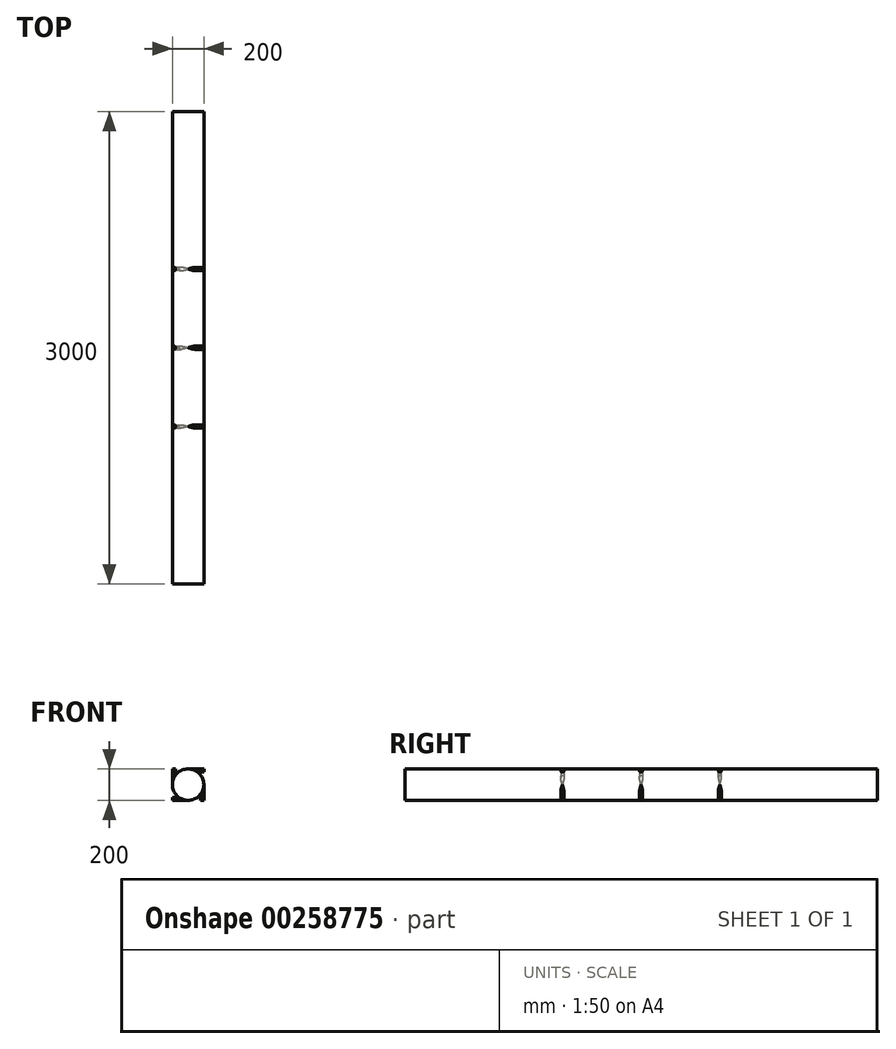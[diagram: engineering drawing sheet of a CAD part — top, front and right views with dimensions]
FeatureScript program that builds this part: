
annotation { "Feature Type Name" : "Feature", "Feature Type Description" : "" }
export const myFeature = defineFeature(function(context is Context, id is Id, definition is map)
    precondition{}
    {
        {
            var Q0;
            Q0=qCreatedBy(makeId("Front.planeOp"),FACE);
            var sketch = newSketch(context, id + "F0", { "sketchPlane" : qUnion([Q0])});
            skCircle(sketch, "E0", {"center": v(0, 0) * mm, "radius": 100 * mm});
            skSolve(sketch);
        }
        {
            var Q0;
            Q0=makeQuery(id+"F0.imprint","IMPRINT",FACE,{"disambiguationData":[TD([[makeQuery(id+"F0.imprint","IMPRINT",EDGE,{"derivedFrom":sQuery(id+"F0.wireOp",EDGE,"E0")}),1.0]])]});
            extrude(context, id + "F1", {"entities" : qUnion([Q0]), "oppositeDirection" : true, "depth" : 3000 * mm});
        }
        {
            var Q0;
            Q0=qCreatedBy(makeId("Front.planeOp"),FACE);
            cPlane(context, id + "F2", {"entities" : qUnion([Q0]), "cplaneType" : CPlaneType.OFFSET, "offset" : 1000 * mm, "oppositeDirection" : true, "width" : 150 * mm, "height" : 150 * mm});
        }
        {
            var Q0;
            Q0=qCreatedBy(makeId("Front.planeOp"),FACE);
            cPlane(context, id + "F3", {"entities" : qUnion([Q0]), "cplaneType" : CPlaneType.OFFSET, "offset" : 1500 * mm, "oppositeDirection" : true, "width" : 150 * mm, "height" : 150 * mm});
        }
        {
            var Q0;
            Q0=qCreatedBy(makeId("Front.planeOp"),FACE);
            cPlane(context, id + "F4", {"entities" : qUnion([Q0]), "cplaneType" : CPlaneType.OFFSET, "offset" : 2000 * mm, "oppositeDirection" : true, "width" : 150 * mm, "height" : 150 * mm});
        }
        {
            var Q0;
            Q0=qCreatedBy(id+"F2.planeOp",FACE);
            var sketch = newSketch(context, id + "F5", { "sketchPlane" : qUnion([Q0])});
            skLineSegment(sketch, "E1.bottom", {"start": v(0, 100) * mm, "end": v(100, 100) * mm});
            skLineSegment(sketch, "E1.top", {"start": v(0, 90) * mm, "end": v(100, 90) * mm});
            skLineSegment(sketch, "E1.left", {"start": v(0, 100) * mm, "end": v(0, 90) * mm});
            skLineSegment(sketch, "E1.right", {"start": v(100, 100) * mm, "end": v(100, 90) * mm});
            skPoint(sketch, "E2.center", {"position": v(0, 50) * mm});
            skLineSegment(sketch, "E3.1.0", {"start": v(-100, 0) * mm, "end": v(-100, 100) * mm});
            skLineSegment(sketch, "E3.1.1", {"start": v(-90, 0) * mm, "end": v(-90, 100) * mm});
            skLineSegment(sketch, "E3.1.2", {"start": v(-100, 100) * mm, "end": v(-90, 100) * mm});
            skLineSegment(sketch, "E3.1.3", {"start": v(-100, 0) * mm, "end": v(-90, 0) * mm});
            skLineSegment(sketch, "E3.2.0", {"start": v(0, -100) * mm, "end": v(-100, -100) * mm});
            skLineSegment(sketch, "E3.2.1", {"start": v(0, -90) * mm, "end": v(-100, -90) * mm});
            skLineSegment(sketch, "E3.2.2", {"start": v(-100, -100) * mm, "end": v(-100, -90) * mm});
            skLineSegment(sketch, "E3.2.3", {"start": v(0, -100) * mm, "end": v(0, -90) * mm});
            skLineSegment(sketch, "E3.3.0", {"start": v(100, 0) * mm, "end": v(100, -100) * mm});
            skLineSegment(sketch, "E3.3.1", {"start": v(90, 0) * mm, "end": v(90, -100) * mm});
            skLineSegment(sketch, "E3.3.2", {"start": v(100, -100) * mm, "end": v(90, -100) * mm});
            skLineSegment(sketch, "E3.3.3", {"start": v(100, 0) * mm, "end": v(90, 0) * mm});
            skPoint(sketch, "E3.center", {"position": v(0, 0) * mm});
            skSolve(sketch);
        }
        {
            var Q0;
            Q0=makeQuery(id+"F5.imprint","IMPRINT",FACE,{"disambiguationData":[TD([[makeQuery(id+"F5.imprint","IMPRINT",EDGE,{"derivedFrom":sQuery(id+"F5.wireOp",EDGE,"E1.bottom")}),-1.0]])]});
            var Q1;
            Q1=sQuery(id+"F5.wireOp",EDGE,"E1.top");
            revolve(context, id + "F6", {"operationType" : NewBodyOperationType.ADD, "entities" : qUnion([Q0]), "axis" : qUnion([Q1]), "revolveType" : RevolveType.FULL});
        }
        {
            var Q0;
            Q0=makeQuery(id+"F5.imprint","IMPRINT",FACE,{"disambiguationData":[TD([[makeQuery(id+"F5.imprint","IMPRINT",EDGE,{"derivedFrom":sQuery(id+"F5.wireOp",EDGE,"E3.1.0")}),-1.0]])]});
            var Q1;
            Q1=sQuery(id+"F5.wireOp",EDGE,"E3.1.1");
            revolve(context, id + "F7", {"operationType" : NewBodyOperationType.ADD, "entities" : qUnion([Q0]), "axis" : qUnion([Q1]), "revolveType" : RevolveType.FULL});
        }
        {
            var Q0;
            Q0=makeQuery(id+"F5.imprint","IMPRINT",FACE,{"disambiguationData":[TD([[makeQuery(id+"F5.imprint","IMPRINT",EDGE,{"derivedFrom":sQuery(id+"F5.wireOp",EDGE,"E3.2.0")}),-1.0]])]});
            var Q1;
            Q1=sQuery(id+"F5.wireOp",EDGE,"E3.2.1");
            revolve(context, id + "F8", {"operationType" : NewBodyOperationType.ADD, "entities" : qUnion([Q0]), "axis" : qUnion([Q1]), "revolveType" : RevolveType.FULL});
        }
        {
            var Q0;
            Q0=makeQuery(id+"F5.imprint","IMPRINT",FACE,{"disambiguationData":[TD([[makeQuery(id+"F5.imprint","IMPRINT",EDGE,{"derivedFrom":sQuery(id+"F5.wireOp",EDGE,"E3.3.0")}),-1.0]])]});
            var Q1;
            Q1=sQuery(id+"F5.wireOp",EDGE,"E3.3.1");
            revolve(context, id + "F9", {"operationType" : NewBodyOperationType.ADD, "entities" : qUnion([Q0]), "axis" : qUnion([Q1]), "revolveType" : RevolveType.FULL});
        }
        {
            var Q0;
            Q0=qCreatedBy(id+"F3.planeOp",FACE);
            var sketch = newSketch(context, id + "F10", { "sketchPlane" : qUnion([Q0])});
            skLineSegment(sketch, "E4.bottom", {"start": v(0, 100) * mm, "end": v(100, 100) * mm});
            skLineSegment(sketch, "E4.top", {"start": v(0, 90) * mm, "end": v(100, 90) * mm});
            skLineSegment(sketch, "E4.left", {"start": v(0, 100) * mm, "end": v(0, 90) * mm});
            skLineSegment(sketch, "E4.right", {"start": v(100, 100) * mm, "end": v(100, 90) * mm});
            skLineSegment(sketch, "E5.1.0", {"start": v(-100, 0) * mm, "end": v(-100, 100) * mm});
            skLineSegment(sketch, "E5.1.1", {"start": v(-90, 0) * mm, "end": v(-90, 100) * mm});
            skLineSegment(sketch, "E5.1.2", {"start": v(-100, 100) * mm, "end": v(-90, 100) * mm});
            skLineSegment(sketch, "E5.1.3", {"start": v(-100, 0) * mm, "end": v(-90, 0) * mm});
            skLineSegment(sketch, "E5.2.0", {"start": v(0, -100) * mm, "end": v(-100, -100) * mm});
            skLineSegment(sketch, "E5.2.1", {"start": v(0, -90) * mm, "end": v(-100, -90) * mm});
            skLineSegment(sketch, "E5.2.2", {"start": v(-100, -100) * mm, "end": v(-100, -90) * mm});
            skLineSegment(sketch, "E5.2.3", {"start": v(0, -100) * mm, "end": v(0, -90) * mm});
            skLineSegment(sketch, "E5.3.0", {"start": v(100, 0) * mm, "end": v(100, -100) * mm});
            skLineSegment(sketch, "E5.3.1", {"start": v(90, 0) * mm, "end": v(90, -100) * mm});
            skLineSegment(sketch, "E5.3.2", {"start": v(100, -100) * mm, "end": v(90, -100) * mm});
            skLineSegment(sketch, "E5.3.3", {"start": v(100, 0) * mm, "end": v(90, 0) * mm});
            skPoint(sketch, "E5.center", {"position": v(0, 0) * mm});
            skSolve(sketch);
        }
        {
            var Q0;
            Q0=makeQuery(id+"F10.imprint","IMPRINT",FACE,{"disambiguationData":[TD([[makeQuery(id+"F10.imprint","IMPRINT",EDGE,{"derivedFrom":sQuery(id+"F10.wireOp",EDGE,"E4.bottom")}),-1.0]])]});
            var Q1;
            Q1=sQuery(id+"F10.wireOp",EDGE,"E4.top");
            revolve(context, id + "F11", {"operationType" : NewBodyOperationType.ADD, "entities" : qUnion([Q0]), "axis" : qUnion([Q1]), "revolveType" : RevolveType.FULL});
        }
        {
            var Q0;
            Q0=makeQuery(id+"F10.imprint","IMPRINT",FACE,{"disambiguationData":[TD([[makeQuery(id+"F10.imprint","IMPRINT",EDGE,{"derivedFrom":sQuery(id+"F10.wireOp",EDGE,"E5.3.0")}),-1.0]])]});
            var Q1;
            Q1=sQuery(id+"F10.wireOp",EDGE,"E5.3.1");
            revolve(context, id + "F12", {"operationType" : NewBodyOperationType.ADD, "entities" : qUnion([Q0]), "axis" : qUnion([Q1]), "revolveType" : RevolveType.FULL});
        }
        {
            var Q0;
            Q0=makeQuery(id+"F10.imprint","IMPRINT",FACE,{"disambiguationData":[TD([[makeQuery(id+"F10.imprint","IMPRINT",EDGE,{"derivedFrom":sQuery(id+"F10.wireOp",EDGE,"E5.1.0")}),-1.0]])]});
            var Q1;
            Q1=sQuery(id+"F10.wireOp",EDGE,"E5.1.1");
            revolve(context, id + "F13", {"operationType" : NewBodyOperationType.ADD, "entities" : qUnion([Q0]), "axis" : qUnion([Q1]), "revolveType" : RevolveType.FULL});
        }
        {
            var Q0;
            Q0=makeQuery(id+"F10.imprint","IMPRINT",FACE,{"disambiguationData":[TD([[makeQuery(id+"F10.imprint","IMPRINT",EDGE,{"derivedFrom":sQuery(id+"F10.wireOp",EDGE,"E5.2.0")}),-1.0]])]});
            var Q1;
            Q1=sQuery(id+"F10.wireOp",EDGE,"E5.2.1");
            revolve(context, id + "F14", {"operationType" : NewBodyOperationType.ADD, "entities" : qUnion([Q0]), "axis" : qUnion([Q1]), "revolveType" : RevolveType.FULL});
        }
        {
            var Q0;
            Q0=qCreatedBy(id+"F4.planeOp",FACE);
            var sketch = newSketch(context, id + "F15", { "sketchPlane" : qUnion([Q0])});
            skLineSegment(sketch, "E6", {"start": v(0, 100) * mm, "end": v(100, 100) * mm});
            skLineSegment(sketch, "E7", {"start": v(100, 100) * mm, "end": v(100, 90) * mm});
            skLineSegment(sketch, "E8", {"start": v(100, 90) * mm, "end": v(0, 90) * mm});
            skLineSegment(sketch, "E9", {"start": v(0, 90) * mm, "end": v(0, 100) * mm});
            skLineSegment(sketch, "E10.1.0", {"start": v(-90, 0) * mm, "end": v(-100, 0) * mm});
            skLineSegment(sketch, "E10.1.1", {"start": v(-90, 100) * mm, "end": v(-90, 0) * mm});
            skLineSegment(sketch, "E10.1.2", {"start": v(-100, 0) * mm, "end": v(-100, 100) * mm});
            skLineSegment(sketch, "E10.1.3", {"start": v(-100, 100) * mm, "end": v(-90, 100) * mm});
            skLineSegment(sketch, "E10.2.0", {"start": v(0, -90) * mm, "end": v(0, -100) * mm});
            skLineSegment(sketch, "E10.2.1", {"start": v(-100, -90) * mm, "end": v(0, -90) * mm});
            skLineSegment(sketch, "E10.2.2", {"start": v(0, -100) * mm, "end": v(-100, -100) * mm});
            skLineSegment(sketch, "E10.2.3", {"start": v(-100, -100) * mm, "end": v(-100, -90) * mm});
            skLineSegment(sketch, "E10.3.0", {"start": v(90, 0) * mm, "end": v(100, 0) * mm});
            skLineSegment(sketch, "E10.3.1", {"start": v(90, -100) * mm, "end": v(90, 0) * mm});
            skLineSegment(sketch, "E10.3.2", {"start": v(100, 0) * mm, "end": v(100, -100) * mm});
            skLineSegment(sketch, "E10.3.3", {"start": v(100, -100) * mm, "end": v(90, -100) * mm});
            skPoint(sketch, "E10.center", {"position": v(0, 0) * mm});
            skSolve(sketch);
        }
        {
            var Q0;
            Q0=makeQuery(id+"F15.imprint","IMPRINT",FACE,{"disambiguationData":[TD([[makeQuery(id+"F15.imprint","IMPRINT",EDGE,{"derivedFrom":sQuery(id+"F15.wireOp",EDGE,"E6")}),-1.0]])]});
            var Q1;
            Q1=sQuery(id+"F15.wireOp",EDGE,"E8");
            revolve(context, id + "F16", {"operationType" : NewBodyOperationType.ADD, "entities" : qUnion([Q0]), "axis" : qUnion([Q1]), "revolveType" : RevolveType.FULL});
        }
        {
            var Q0;
            Q0=makeQuery(id+"F15.imprint","IMPRINT",FACE,{"disambiguationData":[TD([[makeQuery(id+"F15.imprint","IMPRINT",EDGE,{"derivedFrom":sQuery(id+"F15.wireOp",EDGE,"E10.3.0")}),-1.0]])]});
            var Q1;
            Q1=sQuery(id+"F15.wireOp",EDGE,"E10.3.1");
            revolve(context, id + "F17", {"operationType" : NewBodyOperationType.ADD, "entities" : qUnion([Q0]), "axis" : qUnion([Q1]), "revolveType" : RevolveType.FULL});
        }
        {
            var Q0;
            Q0=makeQuery(id+"F15.imprint","IMPRINT",FACE,{"disambiguationData":[TD([[makeQuery(id+"F15.imprint","IMPRINT",EDGE,{"derivedFrom":sQuery(id+"F15.wireOp",EDGE,"E10.1.0")}),-1.0]])]});
            var Q1;
            Q1=sQuery(id+"F15.wireOp",EDGE,"E10.1.1");
            revolve(context, id + "F18", {"operationType" : NewBodyOperationType.ADD, "entities" : qUnion([Q0]), "axis" : qUnion([Q1]), "revolveType" : RevolveType.FULL});
        }
        {
            var Q0;
            Q0=makeQuery(id+"F15.imprint","IMPRINT",FACE,{"disambiguationData":[TD([[makeQuery(id+"F15.imprint","IMPRINT",EDGE,{"derivedFrom":sQuery(id+"F15.wireOp",EDGE,"E10.2.0")}),-1.0]])]});
            var Q1;
            Q1=sQuery(id+"F15.wireOp",EDGE,"E10.2.1");
            revolve(context, id + "F19", {"operationType" : NewBodyOperationType.ADD, "entities" : qUnion([Q0]), "axis" : qUnion([Q1]), "revolveType" : RevolveType.FULL});
        }
    });
